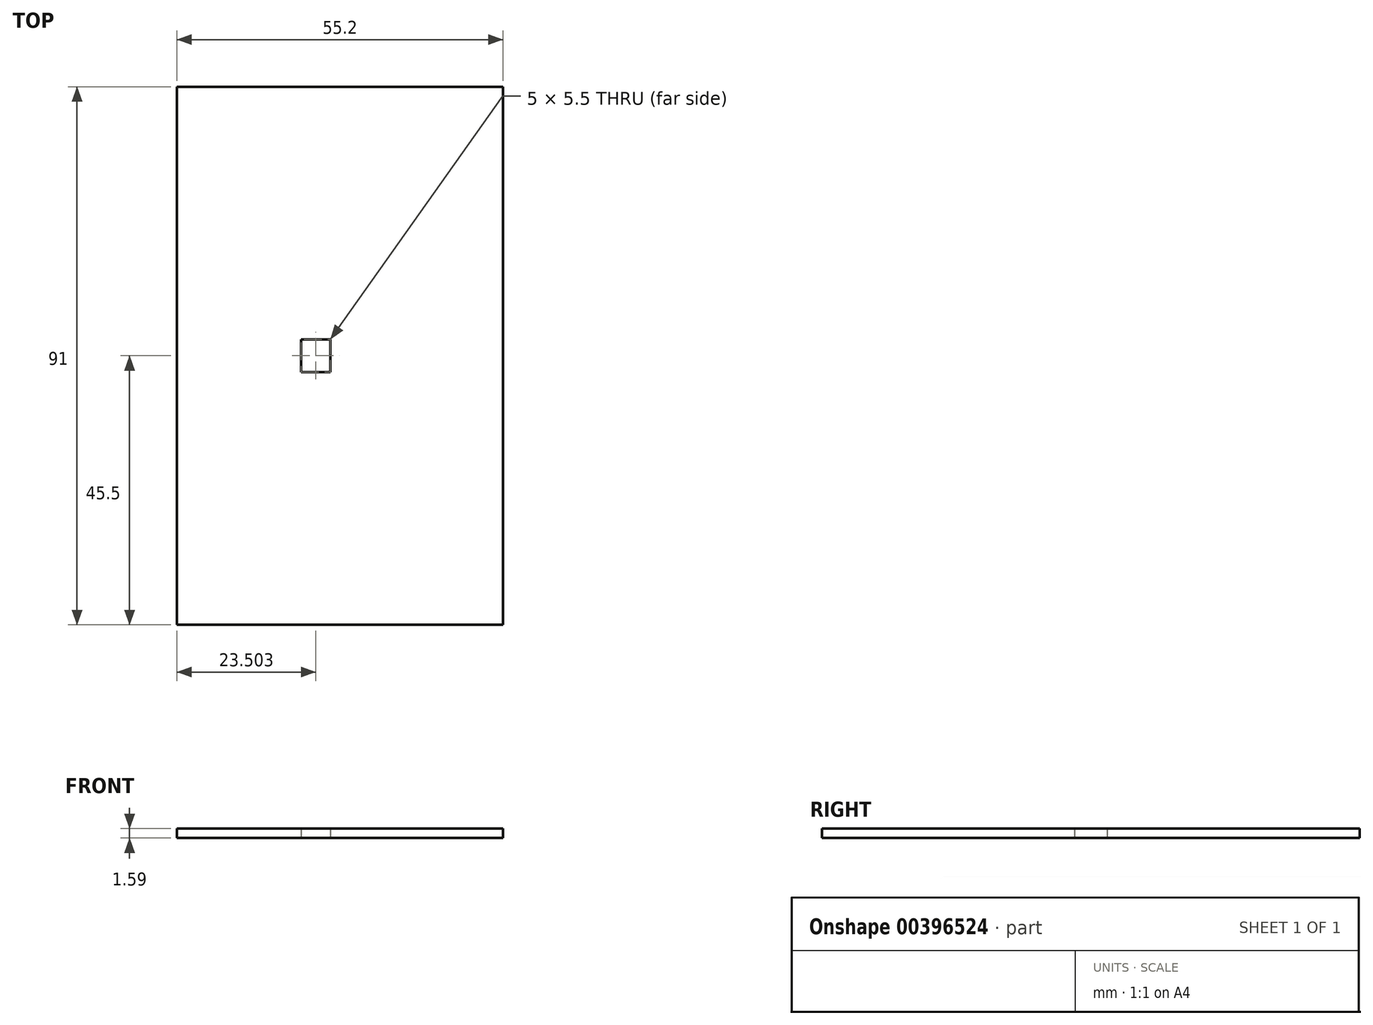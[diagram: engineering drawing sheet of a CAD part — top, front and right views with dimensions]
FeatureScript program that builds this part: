
annotation { "Feature Type Name" : "Feature", "Feature Type Description" : "" }
export const myFeature = defineFeature(function(context is Context, id is Id, definition is map)
    precondition{}
    {
        {
            var Q0;
            Q0=qCreatedBy(makeId("Top.planeOp"),FACE);
            var sketch = newSketch(context, id + "F0", { "sketchPlane" : qUnion([Q0])});
            skLineSegment(sketch, "E0.bottom", {"start": v(27.6, -45.5) * mm, "end": v(-27.6, -45.5) * mm});
            skLineSegment(sketch, "E0.top", {"start": v(27.6, 45.5) * mm, "end": v(-27.6, 45.5) * mm});
            skLineSegment(sketch, "E0.left", {"start": v(27.6, -45.5) * mm, "end": v(27.6, 45.5) * mm});
            skLineSegment(sketch, "E0.right", {"start": v(-27.6, -45.5) * mm, "end": v(-27.6, 45.5) * mm});
            skPoint(sketch, "E0.middle", {"position": v(0, 0) * mm});
            skLineSegment(sketch, "E1.bottom", {"start": v(-6.6, 2.75) * mm, "end": v(-1.6, 2.75) * mm});
            skLineSegment(sketch, "E1.top", {"start": v(-6.6, -2.75) * mm, "end": v(-1.6, -2.75) * mm});
            skLineSegment(sketch, "E1.left", {"start": v(-6.6, 2.75) * mm, "end": v(-6.6, -2.75) * mm});
            skLineSegment(sketch, "E1.right", {"start": v(-1.6, 2.75) * mm, "end": v(-1.6, -2.75) * mm});
            skSolve(sketch);
        }
        {
            var Q0;
            Q0=makeQuery(id+"F0.imprint","IMPRINT",FACE,{"disambiguationData":[TD([[makeQuery(id+"F0.imprint","IMPRINT",EDGE,{"derivedFrom":sQuery(id+"F0.wireOp",EDGE,"E0.bottom")}),-1.0]])]});
            extrude(context, id + "F1", {"entities" : qUnion([Q0]), "depth" : 1.59 * mm});
        }
    });
